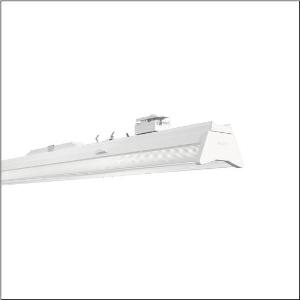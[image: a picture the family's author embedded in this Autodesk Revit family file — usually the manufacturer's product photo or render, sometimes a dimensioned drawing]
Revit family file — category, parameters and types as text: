
# Revit family: licross_r__21_performance_mo_52td16mn4a5g_2767
name_source: partatom
category: Lighting Fixtures
units: mm (PartAtom-declared; Revit-internal decimal feet)

## family parameters
Cut with Voids When Loaded = No
Host = Face
Light Source = No
Part Type = Normal
Room Calculation Point = No
Round Connector Dimension = Use Diameter
Shared = No

## types (1)
- --- (1 x LED, 10890 lm, 60.5 W, 4000K)
    Apparent Load = 61 VA
    CIE Flux Codes = 66 88 96 79 100
    Color Rendering = 80
    Color Temperature = 4000K
    Default Elevation = 1800 mm
    Description = Licross® 21 Performance MO, luminaire insert, of sheet steel, galvanised, coil coated, white, length: 1.500mm, width: 120mm, height: 123mm, LED rated luminous flux: 10.890lm, light colour: 840, control gear: ON/OFF Multilumen, with plug, 3-pole, with phase selection, mains connection: 220..240V, AC, 50/60Hz, rated input power: 61W, halogen-free wiring, primary light control with lens, of plastic, primary optical cover: cover, of PMMA, light emission: direct/indirect distribution, primary light characteristic: symmetric, protection rating (complete): IP54, insulation class (complete): insulation class I (protective earthing), certification: CE, ENEC, UKCA, protection symbol: D if used in an environment with non-conductive dust loads with corresponding accessories, impact resistance: IK06, permissible ambient temperature for indoor applications: -35..+45°C, corresponds to IFS (International Featured Standards) requirements for safety and quality in the food industry, reducing of maximum allowable ambient temperature of 5°C with ceiling mounting, LABS conformity tested according to VDMA 24364:2018-05, packaging unit: 1 piece
    Height = 114 mm
    Lamp = 1 x LED
    Lamp Light Flux = 10890 lm
    Lamp Power = 60.5 W
    Lamp count = 1
    Length = 1500 mm
    Luminous efficacy = 180 lm/W
    Manufacturer = Siteco
    ModVariant = No
    Model = 52TD16MN4A5G
    Mounting Place = Ceiling
    Mounting Type = Pendant
    Number of Poles = 1
    OnlyDefault = Yes
    Power Factor = 1
    Product Name = Licross® 21 Performance MO
    Product group = luminaire insert
    ProductGroupID = 901
    Protection Class = Protection class I
    Protection Degree = IP 54
    RLX_Detail_Level = 1
    RLX_Emergency_Light_Flux = 0 lm
    RLX_Emergency_Type = 0
    RLX_Emergency_Type_DB = No
    RlxData = <blob elided: 31833 chars, md5=da7d4690>
    Socket = socket
    Standby Power = 0 W
    System Light Flux = 10890 lm
    System Power = 61 W
    Type Comments = factory setting: luminous flux: 100 % | (A | C | E) | 140 mA
    Type Image = l_1256138.jpg
    URL = http://relux.com
    VarID = @adj_039351
    Voltage = 0 V
    Weight = 0.00 kg
    Width = 120 mm

## geometry (parser evidence)
native form markers: Blend x4, Sweep x14
no freeform markers — native parametric forms only
